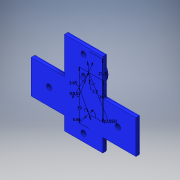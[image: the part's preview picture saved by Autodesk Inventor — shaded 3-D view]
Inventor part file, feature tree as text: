
AUTODESK INVENTOR PART (.ipt)
format: ipt  version: 2016 (Build 200138000, 138)  size: 267,776 bytes
history: native  units: in
note: dims shown in document units (in); Inventor stores cm internally (conversion verified against a paired STEP export)
features: sketch x6, extrude x4, hole x2, fillet x2
ambient origin geometry x8: Origin, YZ Plane, XZ Plane, XY Plane, X Axis, Y Axis, Z Axis, Center Point
bodies: Solid1 (feature_tree)
feature tree (14):
  extrude  "Extrusion1"  Depth=0.5197in
  extrude  "Extrusion10"  Depth=0.0787in
  extrude  "Extrusion11"  Depth=0.2096in TaperAngle=0.0deg
  hole  "Hole2"  [1 undecoded]
  extrude  "Extrusion12"  Depth=0.2953in
  fillet  "Fillet17"  Radius=0.2953in
  fillet  "Fillet18"  Radius=0.2598in
  hole  "Hole4"  [1 undecoded]
  sketch  "Sketch1"  dims[d0=1.6142in d1=0.5197in]
  sketch  "Sketch15"  dims[d2=0.0787in d3=0.0in d79=0.5118in]
  sketch  "Sketch16"  dims[d80=0.5118in d81=0.2096in d82=0.0in]
  sketch  "Sketch17"  dims[d83=0.5118in d84=0.5118in]
  sketch  "Sketch19"  dims[d85=0.562in d86=0.0in d87=0.2953in d88=0.2953in d89=0.2598in]
  sketch  "Sketch20"  dims[d90=0.2598in d91=0.2756in d92=0.1181in d93=0.2953in d94=0.2953in d95=0.1181in d96=0.2598in d97=0.2598in d98=0.2756in d99=0.0787in d100=0.2362in d101=0.1575in d102=0.0787in d103=90.0deg d104=0.1181in d105=0.8108in d108=0.2835in d109=0.748in d110=0.5358in d111=0.0219in d112=0.3622in d113=0.1437in d114=0.5551in d115=0.2224in d116=0.0787in d119=0.8386in d120=0.1181in d121=0.0in d122=0.1181in d123=0.0354in d131=0.0591in d132=0.2362in d133=0.1575in d134=0.0787in d135=90.0deg d136=0.1575in d137=0.8108in]
note: 2 required parameter values undecoded (feature->parameter linkage not recoverable at this tier; creation-order binding heuristic only, values carry confidence <= 0.55)
